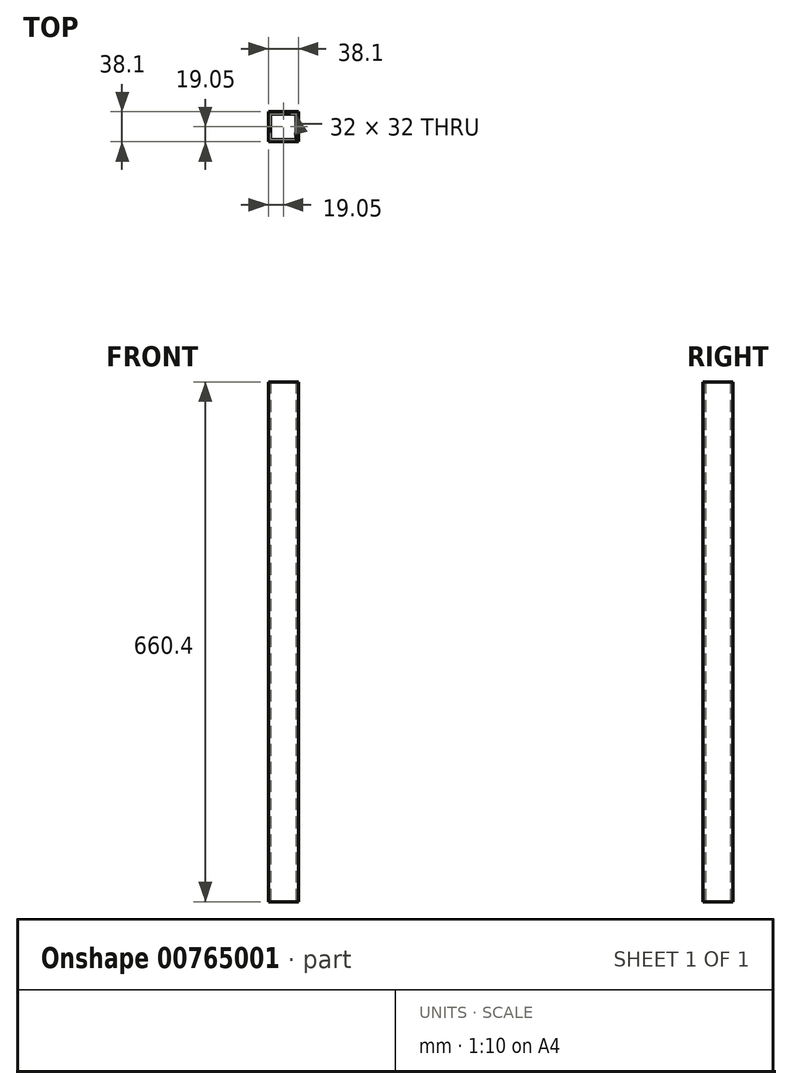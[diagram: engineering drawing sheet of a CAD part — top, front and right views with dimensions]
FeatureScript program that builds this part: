
annotation { "Feature Type Name" : "Feature", "Feature Type Description" : "" }
export const myFeature = defineFeature(function(context is Context, id is Id, definition is map)
    precondition{}
    {
        {
            var Q0;
            Q0=qCreatedBy(makeId("Top.planeOp"),FACE);
            var sketch = newSketch(context, id + "F0", { "sketchPlane" : qUnion([Q0])});
            skLineSegment(sketch, "E0.bottom", {"start": v(19.05, 19.05) * mm, "end": v(-19.05, 19.05) * mm});
            skLineSegment(sketch, "E0.top", {"start": v(19.05, -19.05) * mm, "end": v(-19.05, -19.05) * mm});
            skLineSegment(sketch, "E0.left", {"start": v(19.05, 19.05) * mm, "end": v(19.05, -19.05) * mm});
            skLineSegment(sketch, "E0.right", {"start": v(-19.05, 19.05) * mm, "end": v(-19.05, -19.05) * mm});
            skPoint(sketch, "E0.middle", {"position": v(0, 0) * mm});
            skLineSegment(sketch, "E1.0", {"start": v(16, -16) * mm, "end": v(-16, -16) * mm});
            skLineSegment(sketch, "E1.1", {"start": v(16, 16) * mm, "end": v(16, -16) * mm});
            skLineSegment(sketch, "E1.2", {"start": v(16, 16) * mm, "end": v(-16, 16) * mm});
            skLineSegment(sketch, "E1.3", {"start": v(-16, 16) * mm, "end": v(-16, -16) * mm});
            skSolve(sketch);
        }
        {
            var Q0;
            Q0 = qSketchRegion(id + "F0", true);
            extrude(context, id + "F1", {"entities" : qUnion([Q0]), "depth" : 660.4 * mm, "offsetDistance" : 25.4 * mm});
        }
    });
